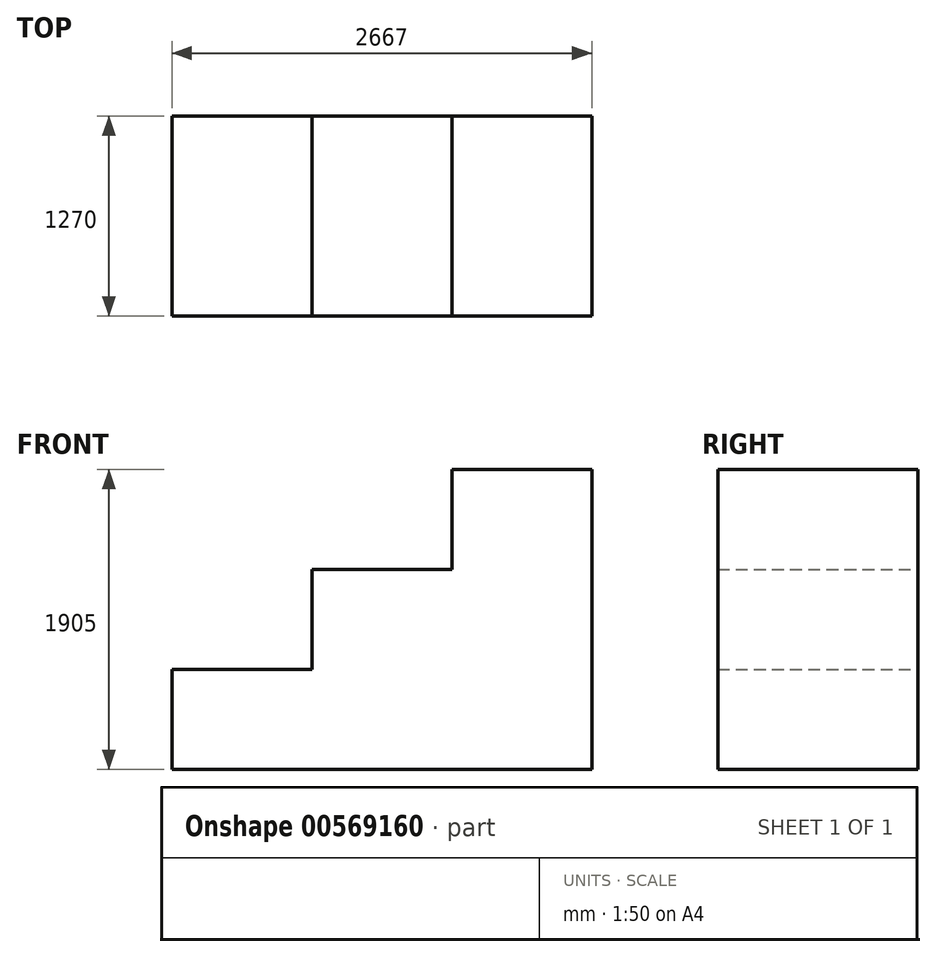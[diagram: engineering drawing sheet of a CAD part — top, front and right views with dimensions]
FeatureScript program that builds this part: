
annotation { "Feature Type Name" : "Feature", "Feature Type Description" : "" }
export const myFeature = defineFeature(function(context is Context, id is Id, definition is map)
    precondition{}
    {
        {
            var Q0;
            Q0=qCreatedBy(makeId("Front.planeOp"),FACE);
            var sketch = newSketch(context, id + "F0", { "sketchPlane" : qUnion([Q0])});
            skLineSegment(sketch, "E0", {"start": v(-41.87, -56.44) * mm, "end": v(2625.13, -56.44) * mm});
            skLineSegment(sketch, "E1", {"start": v(2625.13, -56.44) * mm, "end": v(2625.13, 1848.56) * mm});
            skLineSegment(sketch, "E2", {"start": v(2625.13, 1848.56) * mm, "end": v(1736.13, 1848.56) * mm});
            skLineSegment(sketch, "E3", {"start": v(1736.13, 1848.56) * mm, "end": v(1736.13, 1213.56) * mm});
            skLineSegment(sketch, "E4", {"start": v(1736.13, 1213.56) * mm, "end": v(847.13, 1213.56) * mm});
            skLineSegment(sketch, "E5", {"start": v(847.13, 1213.56) * mm, "end": v(847.13, 578.56) * mm});
            skLineSegment(sketch, "E6", {"start": v(-41.87, 578.56) * mm, "end": v(-41.87, -56.44) * mm});
            skPoint(sketch, "E7.end.orphan", {"position": v(0, 577.31) * mm});
            skLineSegment(sketch, "E8", {"start": v(-41.87, 578.56) * mm, "end": v(847.13, 578.56) * mm});
            skSolve(sketch);
        }
        {
            var Q0;
            Q0 = qSketchRegion(id + "F0", true);
            extrude(context, id + "F1", {"entities" : qUnion([Q0]), "depth" : 1270 * mm, "offsetDistance" : 25.4 * mm});
        }
    });
